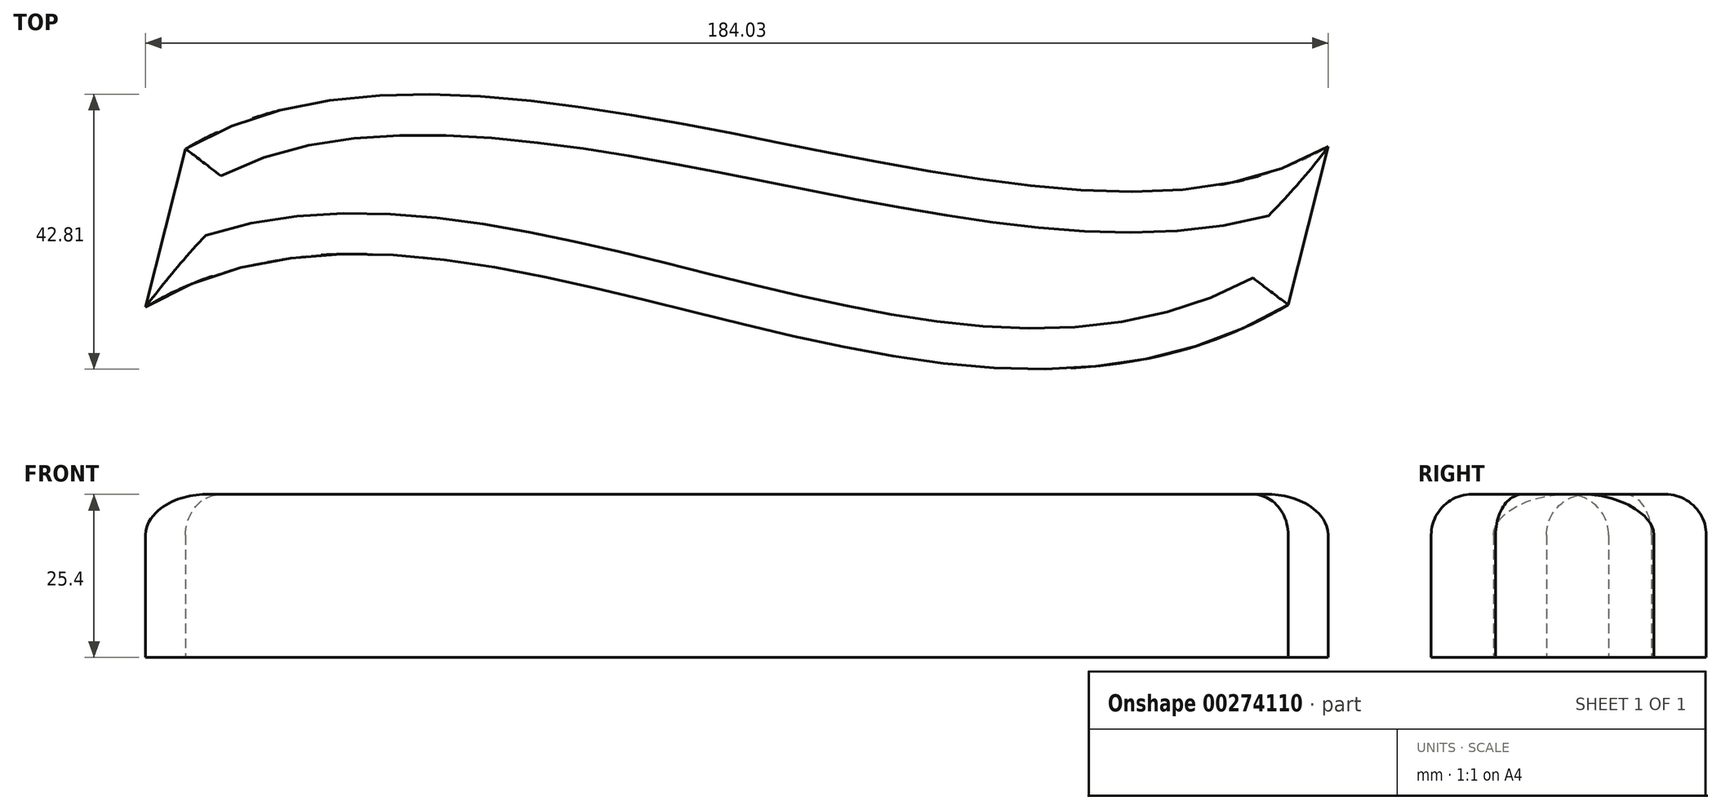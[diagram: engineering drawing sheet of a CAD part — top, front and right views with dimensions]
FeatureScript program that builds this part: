
annotation { "Feature Type Name" : "Feature", "Feature Type Description" : "" }
export const myFeature = defineFeature(function(context is Context, id is Id, definition is map)
    precondition{}
    {
        {
            var Q0;
            Q0=qCreatedBy(makeId("Top.planeOp"),FACE);
            var sketch = newSketch(context, id + "F0", { "sketchPlane" : qUnion([Q0])});
            skLineSegment(sketch, "E0", {"start": v(-23.8, -5.11) * mm, "end": v(-30.02, -29.74) * mm});
            skLineSegment(sketch, "E1", {"start": v(154, -4.75) * mm, "end": v(147.78, -29.37) * mm});
            skFitSpline(sketch, "E2", {"points": [v(-23.8, -5.11) * mm, v(154, -4.75) * mm], "startDerivative": vector(142.03, 84.64) * mm, "endDerivative": vector(127.18, 75.79) * mm});
            skFitSpline(sketch, "E3", {"points": [v(147.78, -29.37) * mm, v(-30.02, -29.74) * mm], "startDerivative": vector(-167.42, -99.77) * mm, "endDerivative": vector(-149.69, -89.2) * mm});
            skLineSegment(sketch, "E4", {"start": v(-23.8, -5.11) * mm, "end": v(23.55, 23.1) * mm});
            skLineSegment(sketch, "E5", {"start": v(19.87, 0) * mm, "end": v(-30.02, -29.74) * mm});
            skLineSegment(sketch, "E6", {"start": v(111.62, -30.01) * mm, "end": v(154, -4.75) * mm});
            skLineSegment(sketch, "E7", {"start": v(147.78, -29.37) * mm, "end": v(91.97, -62.63) * mm});
            skSolve(sketch);
        }
        {
            var Q0;
            Q0=makeQuery(id+"F0.imprint","IMPRINT",FACE,{"disambiguationData":[TD([[makeQuery(id+"F0.imprint","IMPRINT",EDGE,{"derivedFrom":sQuery(id+"F0.wireOp",EDGE,"E0")}),1.0]])]});
            extrude(context, id + "F1", {"entities" : qUnion([Q0]), "depth" : 25.4 * mm});
        }
        {
            var Q0;
            Q0=makeQuery(id+"F1.opExtrude","CAP_EDGE",EDGE,{"disambiguationData":[OSD([sQuery(id+"F0.wireOp",EDGE,"E0")])],"isStart":false});
            var Q1;
            Q1=makeQuery(id+"F1.opExtrude","CAP_EDGE",EDGE,{"disambiguationData":[OSD([sQuery(id+"F0.wireOp",EDGE,"E2")])],"isStart":false});
            var Q2;
            Q2=makeQuery(id+"F1.opExtrude","CAP_EDGE",EDGE,{"disambiguationData":[OSD([sQuery(id+"F0.wireOp",EDGE,"E3")])],"isStart":false});
            var Q3;
            Q3=makeQuery(id+"F1.opExtrude","CAP_EDGE",EDGE,{"disambiguationData":[OSD([sQuery(id+"F0.wireOp",EDGE,"E1")])],"isStart":false});
            fillet(context, id + "F2", {"entities" : qUnion([Q0, Q1, Q2, Q3]), "radius" : 6.35 * mm, "tangentPropagation" : true, "allowEdgeOverflow" : false});
        }
    });
